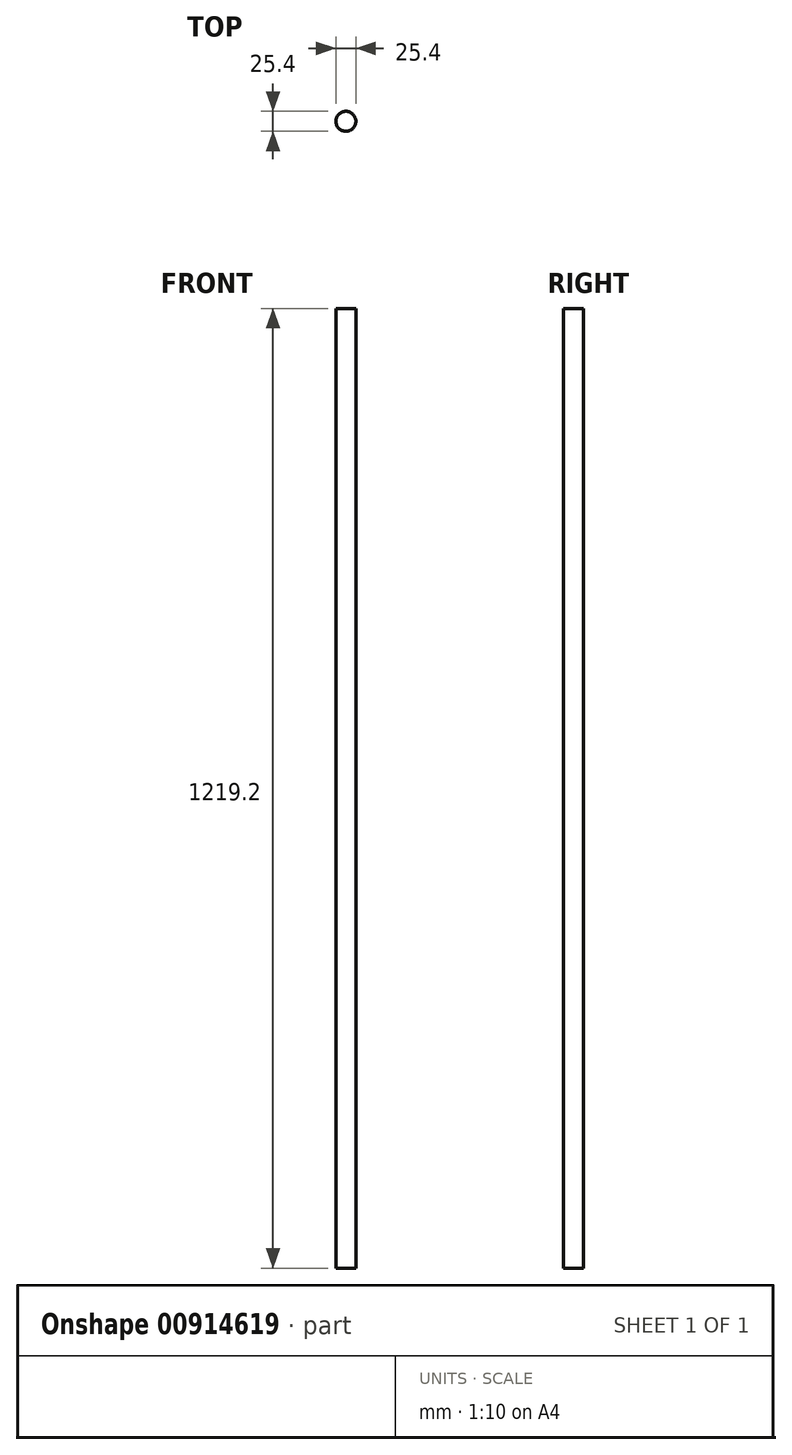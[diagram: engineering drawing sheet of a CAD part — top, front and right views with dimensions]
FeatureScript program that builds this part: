
annotation { "Feature Type Name" : "Feature", "Feature Type Description" : "" }
export const myFeature = defineFeature(function(context is Context, id is Id, definition is map)
    precondition{}
    {
        {
            var Q0;
            Q0=qCreatedBy(makeId("Top.planeOp"),FACE);
            var sketch = newSketch(context, id + "F0", { "sketchPlane" : qUnion([Q0])});
            skCircle(sketch, "E0", {"center": v(0, 0) * mm, "radius": 12.7 * mm});
            skSolve(sketch);
        }
        {
            var Q0;
            Q0 = qSketchRegion(id + "F0", true);
            extrude(context, id + "F1", {"entities" : qUnion([Q0]), "depth" : 1219.2 * mm, "offsetDistance" : 25.4 * mm});
        }
    });
